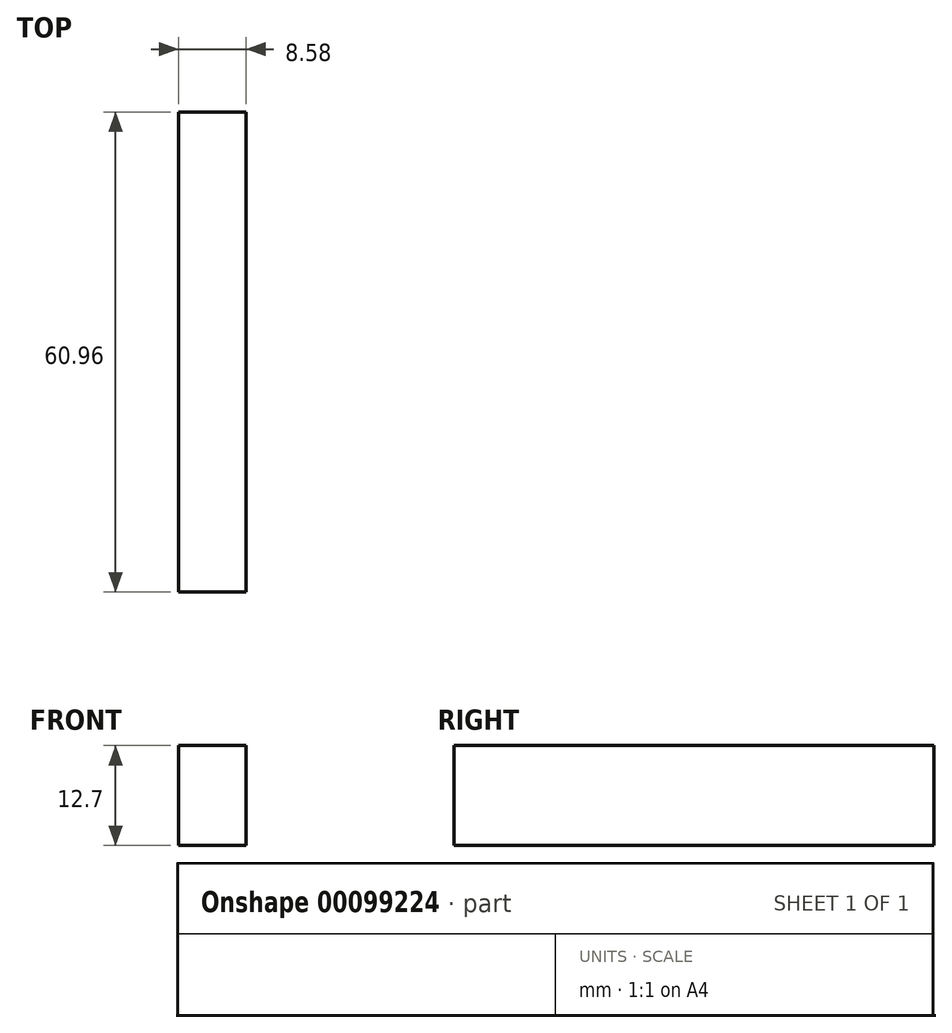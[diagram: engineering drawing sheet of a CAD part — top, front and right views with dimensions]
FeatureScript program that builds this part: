
annotation { "Feature Type Name" : "Feature", "Feature Type Description" : "" }
export const myFeature = defineFeature(function(context is Context, id is Id, definition is map)
    precondition{}
    {
        {
            var Q0;
            Q0=qCreatedBy(makeId("Top.planeOp"),FACE);
            var sketch = newSketch(context, id + "F0", { "sketchPlane" : qUnion([Q0])});
            skLineSegment(sketch, "E0.bottom", {"start": v(4.3, 30.48) * mm, "end": v(-4.3, 30.48) * mm});
            skLineSegment(sketch, "E0.top", {"start": v(4.3, -30.48) * mm, "end": v(-4.3, -30.48) * mm});
            skLineSegment(sketch, "E0.left", {"start": v(4.3, 30.48) * mm, "end": v(4.3, -30.48) * mm});
            skLineSegment(sketch, "E0.right", {"start": v(-4.3, 30.48) * mm, "end": v(-4.3, -30.48) * mm});
            skPoint(sketch, "E0.middle", {"position": v(0, 0) * mm});
            skSolve(sketch);
        }
        {
            var Q0;
            Q0 = qSketchRegion(id + "F0", true);
            extrude(context, id + "F1", {"entities" : qUnion([Q0]), "depth" : 12.7 * mm});
        }
    });
